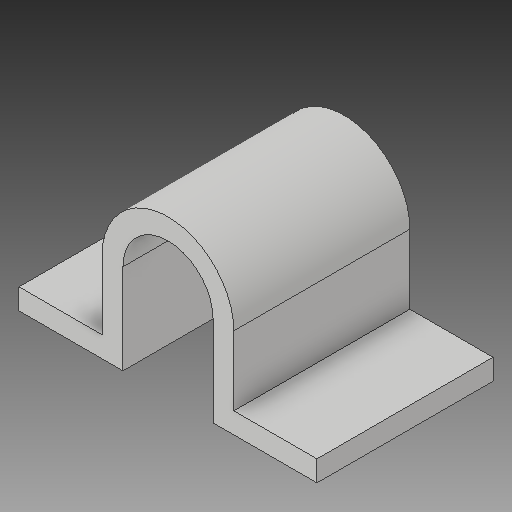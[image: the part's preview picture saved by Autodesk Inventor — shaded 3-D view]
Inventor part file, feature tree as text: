
AUTODESK INVENTOR PART (.ipt)
format: ipt  version: 2018 (Build 220112000, 112)  size: 118,272 bytes
history: native  units: mm
features: extrude x1, sketch x1
ambient origin geometry x8: Origin, YZ Plane, XZ Plane, XY Plane, X Axis, Y Axis, Z Axis, Center Point
bodies: Solid1 (feature_tree)
feature tree (2):
  extrude  "Extrusion1"  Depth=25.4mm TaperAngle=0.0deg
  sketch  "Sketch1"  dims[d10=3.0mm d11=25.4mm d12=0.0mm]
